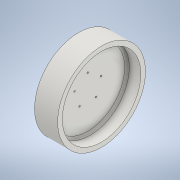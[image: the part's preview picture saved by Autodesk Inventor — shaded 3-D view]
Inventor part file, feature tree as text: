
AUTODESK INVENTOR PART (.ipt)
format: ipt  version: 2022.1 (Build 261234000, 234)  size: 150,528 bytes
history: native  units: mm
features: sketch x3, extrude x2, other x1, fillet x1, hole x1, projected_geometry x1
ambient origin geometry x8: Origin, YZ Plane, XZ Plane, XY Plane, X Axis, Y Axis, Z Axis, Center Point
bodies: Body1 (feature_tree)
feature tree (9):
  other  "Sólido1"
  extrude  "Extrusión1"  Depth=170.0mm
  extrude  "Extrusión2"  Depth=50.0mm
  fillet  "Empalme1"  Radius=12.566371mm
  hole  "Agujero1"  [1 undecoded]
  sketch  "Boceto1"  dims[d0=190.0mm d1=170.0mm]
  sketch  "Boceto4"  dims[d2=50.0mm d3=0.0mm d5=60.0mm d11=12.566371mm]
  sketch  "Boceto7"  dims[d12=12.566371mm d13=12.566371mm d14=12.566371mm d15=20.0mm d16=0.0mm d17=5.0mm d18=2.5mm d19=3.242mm d20=8.0mm d21=4.0mm d22=2.0mm d23=90.0deg d24=8.0mm d25=20.594885mm]
  projected_geometry  "Contorno proyectado1"
note: 1 required parameter value undecoded (feature->parameter linkage not recoverable at this tier; creation-order binding heuristic only, values carry confidence <= 0.55)
